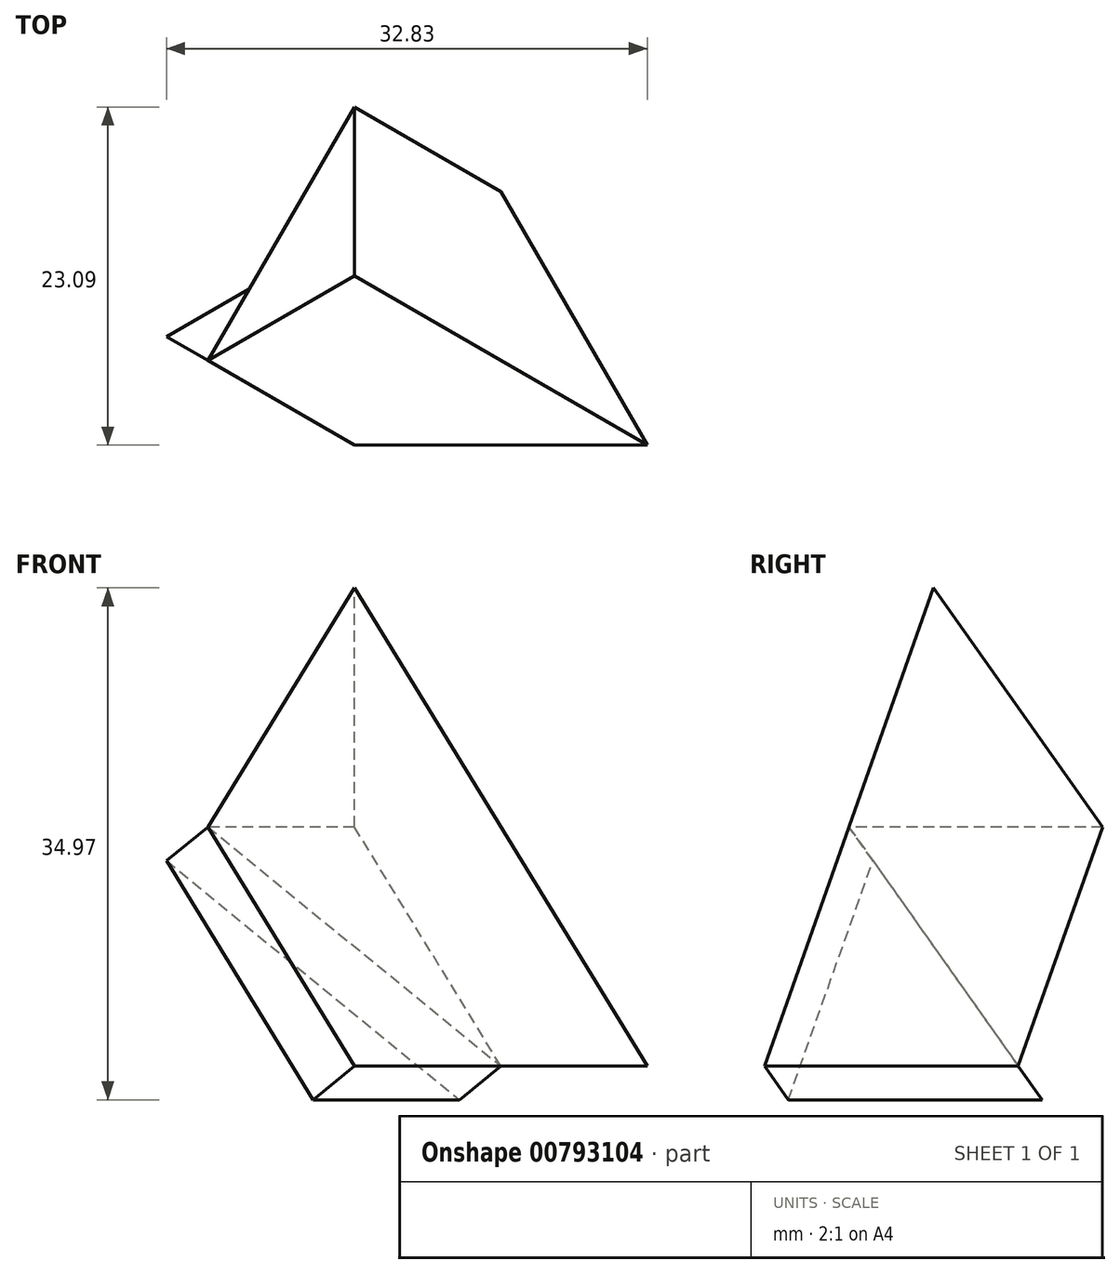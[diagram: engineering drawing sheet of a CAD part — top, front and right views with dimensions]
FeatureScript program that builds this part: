
annotation { "Feature Type Name" : "Feature", "Feature Type Description" : "" }
export const myFeature = defineFeature(function(context is Context, id is Id, definition is map)
    precondition{}
    {
        {
            var Q0;
            Q0=qCreatedBy(makeId("Top.planeOp"),FACE);
            var sketch = newSketch(context, id + "F0", { "sketchPlane" : qUnion([Q0])});
            skLineSegment(sketch, "E0", {"start": v(0, 0) * mm, "end": v(40, 0) * mm});
            skLineSegment(sketch, "E1", {"start": v(40, 0) * mm, "end": v(20, 34.64) * mm});
            skLineSegment(sketch, "E2", {"start": v(20, 34.64) * mm, "end": v(0, 0) * mm});
            skSolve(sketch);
        }
        {
            var Q0;
            Q0=qCreatedBy(makeId("Top.planeOp"),FACE);
            cPlane(context, id + "F1", {"entities" : qUnion([Q0]), "cplaneType" : CPlaneType.OFFSET, "offset" : 32.66 * mm, "width" : 150 * mm, "height" : 150 * mm});
        }
        {
            var Q0;
            Q0=qCreatedBy(id+"F1.planeOp",FACE);
            var sketch = newSketch(context, id + "F2", { "sketchPlane" : qUnion([Q0])});
            skLineSegment(sketch, "E3.0.0", {"start": v(40, 0) * mm, "end": v(20, 34.64) * mm});
            skLineSegment(sketch, "E3.0.1", {"start": v(20, 34.64) * mm, "end": v(0, 0) * mm});
            skLineSegment(sketch, "E3.0.2", {"start": v(0, 0) * mm, "end": v(40, 0) * mm});
            skLineSegment(sketch, "E4", {"start": v(0, 0) * mm, "end": v(30, 17.32) * mm});
            skLineSegment(sketch, "E5", {"start": v(20, 34.64) * mm, "end": v(20, 0) * mm});
            skLineSegment(sketch, "E6", {"start": v(40, 0) * mm, "end": v(10, 17.32) * mm});
            skPoint(sketch, "E7", {"position": v(20, 11.55) * mm});
            skSolve(sketch);
        }
        {
            var Q0;
            Q0=makeQuery(id+"F0.imprint","IMPRINT",FACE,{"disambiguationData":[TD([[makeQuery(id+"F0.imprint","IMPRINT",EDGE,{"derivedFrom":sQuery(id+"F0.wireOp",EDGE,"E0")}),1.0]])]});
            var Q1;
            Q1=sQuery(id+"F2.wireOp",VERTEX,"E7");
            loft(context, id + "F3", {"sheetProfilesArray" : [{ "sheetProfileEntities" : qUnion([Q0]) }, { "sheetProfileEntities" : qUnion([Q1]) }]});
        }
        {
            var Q0;
            {var subQ0=sQuery(id+"F0.wireOp",EDGE,"E1");var subQ1=sQuery(id+"F0.wireOp",EDGE,"E2");var subQ2=sQuery(id+"F0.wireOp",EDGE,"E0");Q0=makeQuery(id+"F3.opLoft","SWEPT_FACE",FACE,{"disambiguationData":[OSD([subQ2,subQ0,subQ1]),TDD([makeQuery(id+"F0.imprint","INTERSECT",VERTEX,{"derivedFrom":[subQ2,subQ0]}),makeQuery(id+"F0.imprint","INTERSECT",VERTEX,{"derivedFrom":[subQ0,subQ1]}),makeQuery(id+"F0.imprint","IMPRINT",EDGE,{"derivedFrom":subQ0})])]});}
            var sketch = newSketch(context, id + "F4", { "sketchPlane" : qUnion([Q0])});
            skLineSegment(sketch, "E8.0.0", {"start": v(21.82, -7.56) * mm, "end": v(-4.36, 22.68) * mm});
            skLineSegment(sketch, "E8.0.1", {"start": v(-4.36, 22.68) * mm, "end": v(-17.46, -15.12) * mm});
            skLineSegment(sketch, "E8.0.2", {"start": v(-17.46, -15.12) * mm, "end": v(21.82, -7.56) * mm});
            skLineSegment(sketch, "E9", {"start": v(2.18, -11.34) * mm, "end": v(8.73, 7.56) * mm});
            skSolve(sketch);
        }
        {
            var Q0;
            {var subQ3=sQuery(id+"F4.wireOp",EDGE,"E9");Q0=makeQuery(id+"F4.imprint","IMPRINT",FACE,{"disambiguationData":[TD([[makeQuery(id+"F4.imprint","IMPRINT",EDGE,{"derivedFrom":subQ3}),-1.0]])]});}
            var Q1;
            {var subQ0=sQuery(id+"F0.wireOp",EDGE,"E2");var subQ1=sQuery(id+"F0.wireOp",EDGE,"E1");var subQ2=sQuery(id+"F0.wireOp",EDGE,"E0");Q1=makeQuery(id+"F3.opLoft","MID_CAP_EDGE",EDGE,{"disambiguationData":[OSD([subQ2,subQ1,subQ0]),TDD([makeQuery(id+"F0.imprint","INTERSECT",VERTEX,{"derivedFrom":[subQ2,subQ0]}),makeQuery(id+"F0.imprint","INTERSECT",VERTEX,{"derivedFrom":[subQ1,subQ0]}),makeQuery(id+"F0.imprint","IMPRINT",EDGE,{"derivedFrom":subQ0})])],"capPos":0.0});}
            sweep(context, id + "F5", {"operationType" : NewBodyOperationType.REMOVE, "profiles" : qUnion([Q0]), "path" : qUnion([Q1])});
        }
        {
            var Q0;
            Q0=makeQuery(id+"F5.boolean.opBoolean","COPY",FACE,{"derivedFrom":makeQuery(id+"F5.opSweep","SWEPT_FACE",FACE,{"disambiguationData":[OSD([sQuery(id+"F0.wireOp",EDGE,"E0"),sQuery(id+"F0.wireOp",EDGE,"E1"),sQuery(id+"F0.wireOp",EDGE,"E2"),sQuery(id+"F4.wireOp",EDGE,"E9")])]})});
            var sketch = newSketch(context, id + "F6", { "sketchPlane" : qUnion([Q0])});
            skLineSegment(sketch, "E10", {"start": v(-31.62, 0) * mm, "end": v(-6.32, -12.65) * mm});
            skLineSegment(sketch, "E11", {"start": v(-6.32, -12.65) * mm, "end": v(-12.65, 6.32) * mm});
            skLineSegment(sketch, "E12", {"start": v(-12.65, 6.32) * mm, "end": v(-25.3, -18.97) * mm});
            skCircle(sketch, "E13", {"center": v(-18.97, -6.32) * mm, "radius": 3.5 * mm});
            skSolve(sketch);
        }
        {
            var Q0;
            {var subQ0=sQuery(id+"F6.wireOp",EDGE,"E13");var subQ1=sQuery(id+"F6.wireOp",EDGE,"E10");var subQ2=makeQuery(id+"F6.imprint","INTERSECT",VERTEX,{"disambiguationData":[OD(0.0)],"derivedFrom":[subQ1,subQ0]});Q0=makeQuery(id+"F6.imprint","IMPRINT",FACE,{"disambiguationData":[TD([[makeQuery(id+"F6.imprint","IMPRINT",EDGE,{"disambiguationData":[TD([[subQ2,-1.0]])],"derivedFrom":subQ1}),1.0]])]});}
            var Q1;
            {var subQ0=sQuery(id+"F6.wireOp",EDGE,"E12");var subQ1=sQuery(id+"F6.wireOp",EDGE,"E10");var subQ2=makeQuery(id+"F6.imprint","INTERSECT",VERTEX,{"derivedFrom":[subQ1,subQ0]});Q1=makeQuery(id+"F6.imprint","IMPRINT",FACE,{"disambiguationData":[TD([[makeQuery(id+"F6.imprint","IMPRINT",EDGE,{"disambiguationData":[TD([[subQ2,-1.0]])],"derivedFrom":subQ1}),1.0]])]});}
            var Q2;
            {var subQ0=sQuery(id+"F6.wireOp",EDGE,"E13");var subQ1=sQuery(id+"F6.wireOp",EDGE,"E10");var subQ2=makeQuery(id+"F6.imprint","INTERSECT",VERTEX,{"disambiguationData":[OD(0.0)],"derivedFrom":[subQ1,subQ0]});Q2=makeQuery(id+"F6.imprint","IMPRINT",FACE,{"disambiguationData":[TD([[makeQuery(id+"F6.imprint","IMPRINT",EDGE,{"disambiguationData":[TD([[subQ2,-1.0]])],"derivedFrom":subQ1}),-1.0]])]});}
            var Q3;
            {var subQ0=sQuery(id+"F6.wireOp",EDGE,"E12");var subQ1=sQuery(id+"F6.wireOp",EDGE,"E10");var subQ2=makeQuery(id+"F6.imprint","INTERSECT",VERTEX,{"derivedFrom":[subQ1,subQ0]});Q3=makeQuery(id+"F6.imprint","IMPRINT",FACE,{"disambiguationData":[TD([[makeQuery(id+"F6.imprint","IMPRINT",EDGE,{"disambiguationData":[TD([[subQ2,-1.0]])],"derivedFrom":subQ1}),-1.0]])]});}
            extrude(context, id + "F7", {"entities" : qUnion([Q0, Q1, Q2, Q3]), "operationType" : NewBodyOperationType.ADD, "depth" : 4 * mm, "offsetDistance" : 25 * mm});
        }
    });
